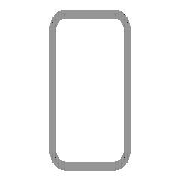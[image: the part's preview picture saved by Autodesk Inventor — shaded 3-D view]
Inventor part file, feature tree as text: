
AUTODESK INVENTOR PART (.ipt)
format: ipt  version: 2025 (Build 290162010, 162A)  size: 134,656 bytes
history: native  units: mm (DEFAULTED — no unit token found)
features: other x4, sketch x1, plane x1
ambient origin geometry x8: Origin, YZ Plane, XZ Plane, XY Plane, X Axis, Y Axis, Z Axis, Center Point
bodies: Solid1 (feature_tree), Body (feature_tree)
feature tree (6):
  parser-record x1  (decoder bookkeeping rows leaked as tree rows — omitted from the tree; the rows remain in map.json)
  other  "Driven Length"
  other  "Start Plane"
  other  "End Plane"
  sketch  "Sketch3"  dims[d3=2906.0mm d4=0.0mm d7=4.0mm d9=40.0mm d11=80.0mm d12=2.0mm d13=-0.0mm d14=2906.0mm d15=20.0mm d16=40.0mm d17=90.0deg d18=2906.0mm]
  plane  "Work Plane3"
